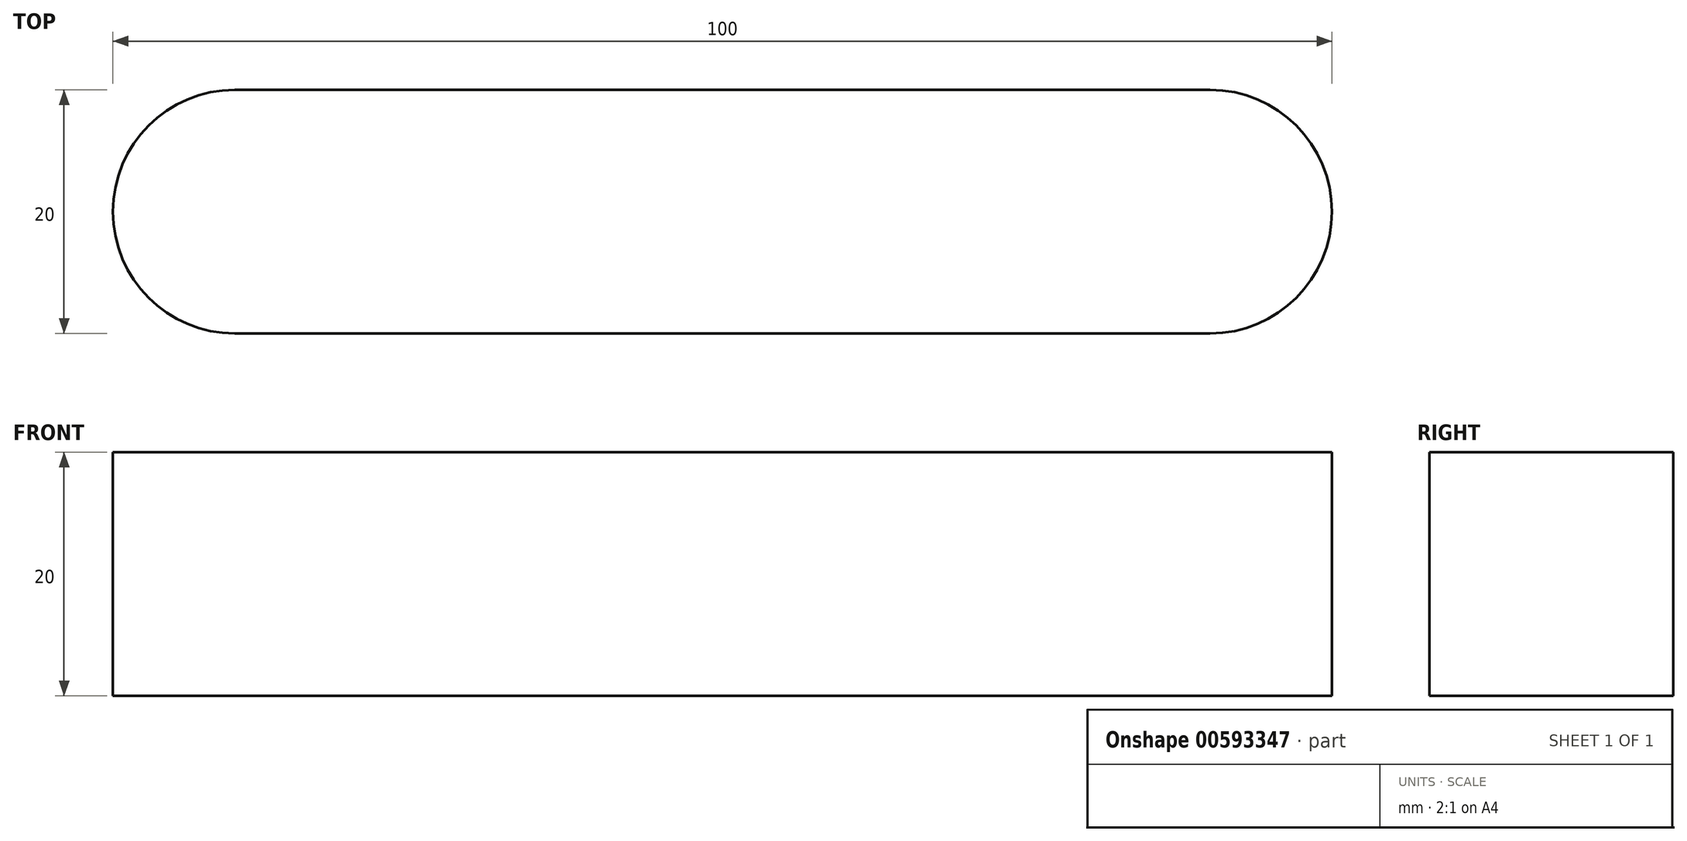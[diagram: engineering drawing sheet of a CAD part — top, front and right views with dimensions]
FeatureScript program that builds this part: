
annotation { "Feature Type Name" : "Feature", "Feature Type Description" : "" }
export const myFeature = defineFeature(function(context is Context, id is Id, definition is map)
    precondition{}
    {
        {
            var Q0;
            Q0=qCreatedBy(makeId("Top.planeOp"),FACE);
            var sketch = newSketch(context, id + "F0", { "sketchPlane" : qUnion([Q0])});
            skLineSegment(sketch, "E0", {"start": v(0, -10) * mm, "end": v(80, -10) * mm});
            skArc(sketch, "E1", {"start": v(80, -10) * mm, "mid": v(90, 0) * mm, "end": v(80, 10) * mm});
            skLineSegment(sketch, "E2", {"start": v(80, 10) * mm, "end": v(0, 10) * mm});
            skArc(sketch, "E3", {"start": v(0, 10) * mm, "mid": v(-10, 0) * mm, "end": v(0, -10) * mm});
            skSolve(sketch);
        }
        {
            var Q0;
            Q0 = qSketchRegion(id + "F0", true);
            extrude(context, id + "F1", {"entities" : qUnion([Q0]), "depth" : 20 * mm, "offsetDistance" : 25 * mm});
        }
    });
